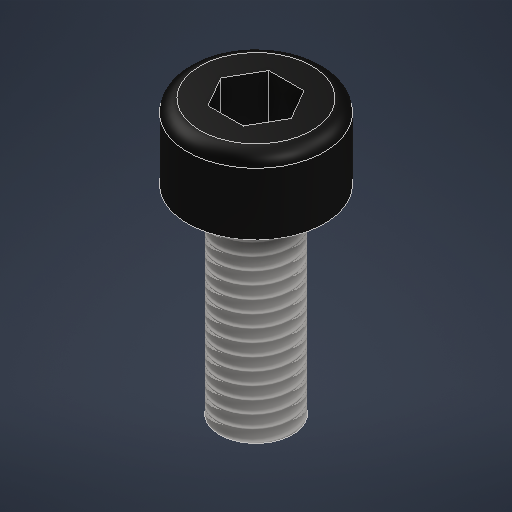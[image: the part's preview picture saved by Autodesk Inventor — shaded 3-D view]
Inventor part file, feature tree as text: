
AUTODESK INVENTOR PART (.ipt)
format: ipt  version: 2025.1 (Build 291241000, 241)  size: 265,728 bytes
history: native  units: mm
features: extrude x3, sketch x1, fillet x1, thread x1
ambient origin geometry x8: Origin, YZ Plane, XZ Plane, XY Plane, X Axis, Y Axis, Z Axis, Center Point
bodies: Solid1 (feature_tree)
feature tree (6):
  sketch  "Sketch1"  dims[d0=2.93mm d1=5.5mm d2=3.0mm d3=0.0mm d4=8.0mm d5=0.0mm d8=2.45mm d9=2.0mm d10=0.0mm d11=0.5mm d12=16.0mm d13=0.0mm]
  extrude  "Extrusion1"  Depth=0.5mm
  extrude  "Extrusion2"  Depth=3.0mm TaperAngle=0.0deg
  extrude  "Extrusion3"  Depth=8.0mm
  fillet  "Fillet1"  [1 undecoded]
  thread  "Thread2"  [1 undecoded]
note: 2 required parameter values undecoded (feature->parameter linkage not recoverable at this tier; creation-order binding heuristic only, values carry confidence <= 0.55)
